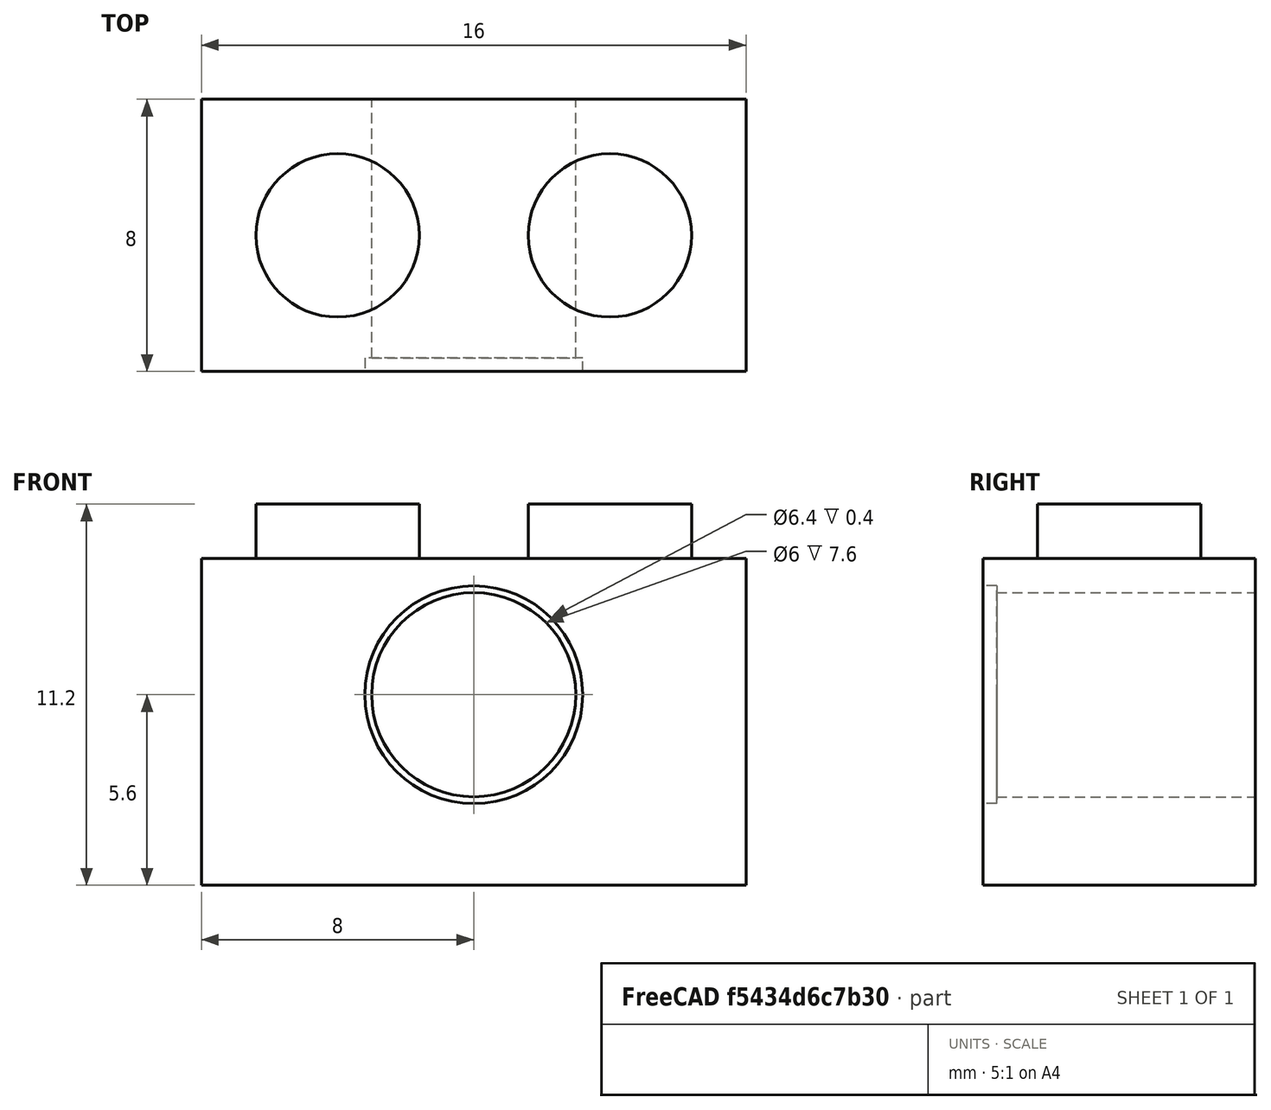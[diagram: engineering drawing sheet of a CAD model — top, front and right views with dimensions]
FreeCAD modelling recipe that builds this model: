
FCSTD DOCUMENT  (FreeCAD 0.18R4 (GitTag))
Label: Block
License: All rights reserved
LicenseURL: http://en.wikipedia.org/wiki/All_rights_reserved
objects: Sketcher::SketchObject×4, PartDesign::Pad×2, PartDesign::Hole×1, PartDesign::Pocket×1, PartDesign::Body×1, Mesh::Feature×1
note: 13 computed .brp shape members not serialized (recipe doc carries the construction recipe); baked Part::Feature solids carry a one-line shape summary decoded from their .brp

FEATURE [Sketcher::SketchObject] Sketch
  MapMode = 5
  Support = -> [XY_Plane]
  sketch-geometry (4):
    g0: LineSegment StartX=0 StartY=0 StartZ=0 EndX=16 EndY=0 EndZ=0
    g1: LineSegment StartX=16 StartY=0 StartZ=0 EndX=16 EndY=8 EndZ=0
    g2: LineSegment StartX=16 StartY=8 StartZ=0 EndX=0 EndY=8 EndZ=0
    g3: LineSegment StartX=0 StartY=8 StartZ=0 EndX=0 EndY=0 EndZ=0
  constraints (11):
    c: Coincident(g0,g1)
    c: Coincident(g1,g2)
    c: Coincident(g2,g3)
    c: Coincident(g3,g0)
    c: Horizontal(g0)
    c: Horizontal(g2)
    c: Vertical(g1)
    c: Vertical(g3)
    c: DistanceX(g0,g0) = 16
    c: DistanceY(g1,g1) = 8
    c: Coincident(g0,g-1)
FEATURE [PartDesign::Pad] Pad
  Length = 9.6
  Length2 = 100
  Profile = -> Sketch
  Type = 0
FEATURE [Sketcher::SketchObject] Sketch001
  MapMode = 5
  Placement = pos=(0,0,0) rot=(1,0,0;1.5708rad)
  Support = -> [Pad]
  sketch-geometry (1):
    g0: Circle CenterX=8 CenterY=5.6 CenterZ=0 NormalX=0 NormalY=0 NormalZ=1 AngleXU=0 Radius=2.4
  constraints (3):
    c: Radius(g0) = 2.4
    c: DistanceX(g-1,g0) = 8
    c: DistanceY(g-1,g0) = 5.6
FEATURE [PartDesign::Hole] Hole
  BaseFeature = -> Pad
  Depth = 25
  DepthType = 0
  Diameter = 6
  DrillPoint = 0
  DrillPointAngle = 118
  HoleCutCountersinkAngle = 90
  HoleCutDepth = 0
  HoleCutDiameter = 0
  HoleCutType = 0
  ModelActualThread = false
  Profile = -> Sketch001
  Tapered = false
  TaperedAngle = 90
  ThreadAngle = 0
  ThreadClass = 0
  ThreadCutOffInner = 0
  ThreadCutOffOuter = 0
  ThreadDirection = 0
  ThreadFit = 0
  ThreadPitch = 0
  ThreadSize = 0
  ThreadType = 0
  Threaded = false
FEATURE [Sketcher::SketchObject] Sketch002
  MapMode = 5
  Placement = pos=(0,0,9.6) rot=(0,0,1;0rad)
  Support = -> [Hole]
  sketch-geometry (2):
    g0: Circle CenterX=4 CenterY=4 CenterZ=0 NormalX=0 NormalY=0 NormalZ=1 AngleXU=0 Radius=2.4
    g1: Circle CenterX=12 CenterY=4 CenterZ=0 NormalX=0 NormalY=0 NormalZ=1 AngleXU=0 Radius=2.4
  constraints (6):
    c: Radius(g1) = 2.4
    c: Radius(g0) = 2.4
    c: Horizontal(g1,g0)
    c: DistanceX(g-1,g0) = 4
    c: DistanceX(g-1,g1) = 12
    c: DistanceY(g-1,g0) = 4
FEATURE [PartDesign::Pad] Pad001
  BaseFeature = -> Hole
  Length = 1.6
  Length2 = 100
  Profile = -> Sketch002
  Type = 0
FEATURE [Sketcher::SketchObject] Sketch003
  MapMode = 5
  Placement = pos=(0,0,0) rot=(1,0,0;1.5708rad)
  Support = -> [Pad001]
  sketch-geometry (1):
    g0: Circle CenterX=8 CenterY=5.6 CenterZ=0 NormalX=0 NormalY=0 NormalZ=1 AngleXU=0 Radius=3.2
  constraints (3):
    c: DistanceX(g-1,g0) = 8
    c: DistanceY(g-1,g0) = 5.6
    c: Radius(g0) = 3.2
FEATURE [PartDesign::Pocket] Pocket
  BaseFeature = -> Pad001
  Length = 0.4
  Length2 = 100
  Profile = -> Sketch003
  Type = 0
FEATURE [PartDesign::Body] Body
  Group = -> [Sketch,Pad,Sketch001,Hole,Sketch002,Pad001,Sketch003,Pocket]
  Origin = -> Origin
  Tip = -> Pocket
FEATURE [Mesh::Feature] Mesh  label="Body (Meshed)"
